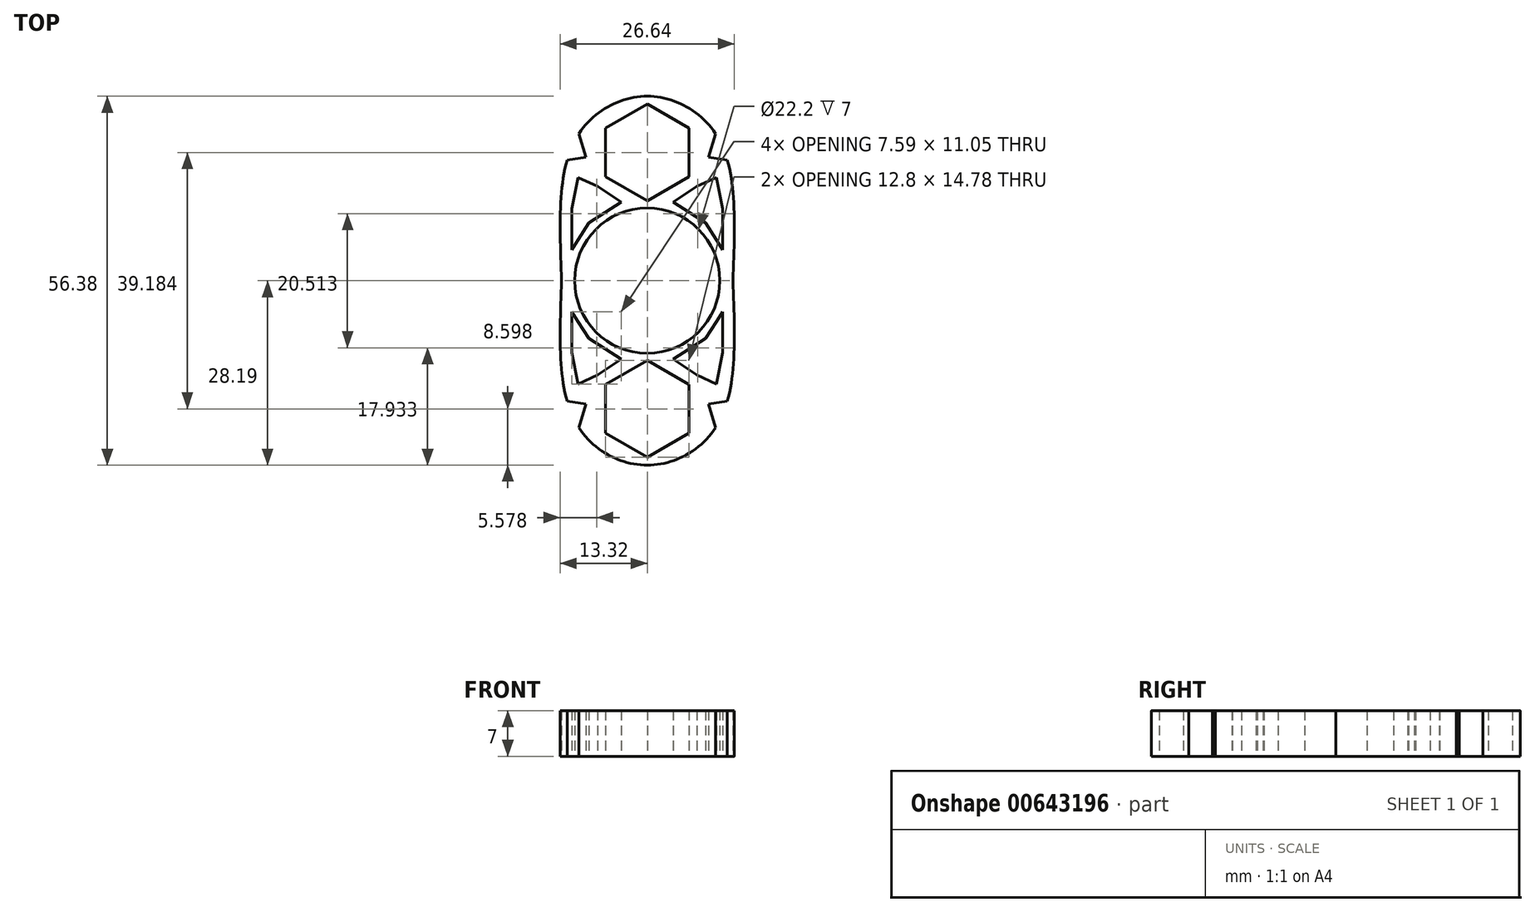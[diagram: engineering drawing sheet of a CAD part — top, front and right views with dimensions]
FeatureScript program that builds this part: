
annotation { "Feature Type Name" : "Feature", "Feature Type Description" : "" }
export const myFeature = defineFeature(function(context is Context, id is Id, definition is map)
    precondition{}
    {
        {
            var Q0;
            Q0=qCreatedBy(makeId("Top.planeOp"),FACE);
            var sketch = newSketch(context, id + "F0", { "sketchPlane" : qUnion([Q0])});
            skCircle(sketch, "E0", {"center": v(0, 0) * mm, "radius": 11.1 * mm});
            skCircle(sketch, "E1.cCircle", {"center": v(0, 19.6) * mm, "radius": 6.4 * mm, "construction": true});
            skLineSegment(sketch, "E1.0", {"start": v(6.4, 23.29) * mm, "end": v(6.4, 15.9) * mm});
            skLineSegment(sketch, "E1.1", {"start": v(6.4, 15.9) * mm, "end": v(0, 12.2) * mm});
            skLineSegment(sketch, "E1.2", {"start": v(0, 12.2) * mm, "end": v(-6.4, 15.9) * mm});
            skLineSegment(sketch, "E1.3", {"start": v(-6.4, 15.9) * mm, "end": v(-6.4, 23.29) * mm});
            skLineSegment(sketch, "E1.4", {"start": v(-6.4, 23.29) * mm, "end": v(0, 26.98) * mm});
            skLineSegment(sketch, "E1.5", {"start": v(0, 26.98) * mm, "end": v(6.4, 23.29) * mm});
            skPoint(sketch, "E1.0.midPoint", {"position": v(6.4, 19.6) * mm});
            skLineSegment(sketch, "E2", {"start": v(-40.43, 30) * mm, "end": v(39.47, 30) * mm, "construction": true});
            skLineSegment(sketch, "E3", {"start": v(39.47, 30) * mm, "end": v(39.47, -30) * mm, "construction": true});
            skLineSegment(sketch, "E4", {"start": v(39.47, -30) * mm, "end": v(-39.28, -30) * mm, "construction": true});
            skFitSpline(sketch, "E5", {"points": [v(0, 28.19) * mm, v(-10.7, 22.08) * mm, v(-13.1, 0) * mm], "startDerivative": vector(-28.16, 0.12) * mm, "endDerivative": vector(1.7, -45.3) * mm});
            skFitSpline(sketch, "E6.MirrorCS", {"points": [v(0, 28.19) * mm, v(10.7, 22.08) * mm, v(13.1, 0) * mm], "startDerivative": vector(28.16, 0.12) * mm, "endDerivative": vector(-1.7, -45.3) * mm});
            skFitSpline(sketch, "E7.MirrorCS", {"points": [v(0, -28.19) * mm, v(-10.7, -22.08) * mm, v(-13.1, 0) * mm], "startDerivative": vector(-28.16, -0.12) * mm, "endDerivative": vector(1.7, 45.3) * mm});
            skFitSpline(sketch, "E8.MirrorCS", {"points": [v(0, -28.19) * mm, v(10.7, -22.08) * mm, v(13.1, 0) * mm], "startDerivative": vector(28.16, -0.12) * mm, "endDerivative": vector(-1.7, 45.3) * mm});
            skLineSegment(sketch, "E9.MirrorCS", {"start": v(-6.4, -15.9) * mm, "end": v(-6.4, -23.29) * mm});
            skPoint(sketch, "E10.MirrorP", {"position": v(6.4, -19.6) * mm});
            skLineSegment(sketch, "E11.MirrorCS", {"start": v(6.4, -23.29) * mm, "end": v(6.4, -15.9) * mm});
            skCircle(sketch, "E12.MirrorC", {"center": v(0, -19.6) * mm, "radius": 6.4 * mm, "construction": true});
            skLineSegment(sketch, "E13.MirrorCS", {"start": v(0, -26.98) * mm, "end": v(6.4, -23.29) * mm});
            skLineSegment(sketch, "E14.MirrorCS", {"start": v(-6.4, -23.29) * mm, "end": v(0, -26.98) * mm});
            skLineSegment(sketch, "E15.MirrorCS", {"start": v(0, -12.2) * mm, "end": v(-6.4, -15.9) * mm});
            skLineSegment(sketch, "E16.MirrorCS", {"start": v(6.4, -15.9) * mm, "end": v(0, -12.2) * mm});
            skLineSegment(sketch, "E17", {"start": v(7.6, 14.42) * mm, "end": v(3.94, 12) * mm});
            skLineSegment(sketch, "E18", {"start": v(3.94, 12) * mm, "end": v(8.93, 8.83) * mm});
            skLineSegment(sketch, "E19", {"start": v(8.93, 8.83) * mm, "end": v(10.58, 6.26) * mm});
            skLineSegment(sketch, "E20", {"start": v(10.58, 6.26) * mm, "end": v(11.54, 4.73) * mm});
            skLineSegment(sketch, "E21", {"start": v(11.54, 4.73) * mm, "end": v(11.54, 11) * mm});
            skLineSegment(sketch, "E22", {"start": v(11.54, 11) * mm, "end": v(10.58, 15.78) * mm});
            skLineSegment(sketch, "E23", {"start": v(10.58, 15.78) * mm, "end": v(7.6, 14.42) * mm});
            skLineSegment(sketch, "E24.MirrorCS", {"start": v(-10.58, 6.26) * mm, "end": v(-11.54, 4.73) * mm});
            skLineSegment(sketch, "E25.MirrorCS", {"start": v(-10.58, 15.78) * mm, "end": v(-7.6, 14.42) * mm});
            skLineSegment(sketch, "E26.MirrorCS", {"start": v(-3.94, 12) * mm, "end": v(-8.93, 8.83) * mm});
            skLineSegment(sketch, "E27.MirrorCS", {"start": v(-7.6, 14.42) * mm, "end": v(-3.94, 12) * mm});
            skLineSegment(sketch, "E28.MirrorCS", {"start": v(-8.93, 8.83) * mm, "end": v(-10.58, 6.26) * mm});
            skLineSegment(sketch, "E29.MirrorCS", {"start": v(-11.54, 11) * mm, "end": v(-10.58, 15.78) * mm});
            skLineSegment(sketch, "E30.MirrorCS", {"start": v(-11.54, 4.73) * mm, "end": v(-11.54, 11) * mm});
            skLineSegment(sketch, "E31.MirrorCS", {"start": v(-10.58, -6.26) * mm, "end": v(-11.54, -4.73) * mm});
            skLineSegment(sketch, "E32.MirrorCS", {"start": v(-3.94, -12) * mm, "end": v(-8.93, -8.83) * mm});
            skLineSegment(sketch, "E33.MirrorCS", {"start": v(-11.54, -4.73) * mm, "end": v(-11.54, -11) * mm});
            skLineSegment(sketch, "E34.MirrorCS", {"start": v(-10.58, -15.78) * mm, "end": v(-7.6, -14.42) * mm});
            skLineSegment(sketch, "E35.MirrorCS", {"start": v(-8.93, -8.83) * mm, "end": v(-10.58, -6.26) * mm});
            skLineSegment(sketch, "E36.MirrorCS", {"start": v(-7.6, -14.42) * mm, "end": v(-3.94, -12) * mm});
            skLineSegment(sketch, "E37.MirrorCS", {"start": v(-11.54, -11) * mm, "end": v(-10.58, -15.78) * mm});
            skLineSegment(sketch, "E38.MirrorCS", {"start": v(10.58, -6.26) * mm, "end": v(11.54, -4.73) * mm});
            skLineSegment(sketch, "E39.MirrorCS", {"start": v(10.58, -15.78) * mm, "end": v(7.6, -14.42) * mm});
            skLineSegment(sketch, "E40.MirrorCS", {"start": v(8.93, -8.83) * mm, "end": v(10.58, -6.26) * mm});
            skLineSegment(sketch, "E41.MirrorCS", {"start": v(11.54, -4.73) * mm, "end": v(11.54, -11) * mm});
            skLineSegment(sketch, "E42.MirrorCS", {"start": v(11.54, -11) * mm, "end": v(10.58, -15.78) * mm});
            skLineSegment(sketch, "E43.MirrorCS", {"start": v(7.6, -14.42) * mm, "end": v(3.94, -12) * mm});
            skLineSegment(sketch, "E44.MirrorCS", {"start": v(3.94, -12) * mm, "end": v(8.93, -8.83) * mm});
            skLineSegment(sketch, "E45", {"start": v(-14.85, 18.06) * mm, "end": v(-9.4, 18.84) * mm});
            skLineSegment(sketch, "E46", {"start": v(-9.4, 18.84) * mm, "end": v(-11.31, 25.3) * mm});
            skLineSegment(sketch, "E47", {"start": v(-11.31, 25.3) * mm, "end": v(-14.85, 18.06) * mm});
            skLineSegment(sketch, "E48.MirrorCS", {"start": v(9.4, 18.84) * mm, "end": v(11.31, 25.3) * mm});
            skLineSegment(sketch, "E49.MirrorCS", {"start": v(11.31, 25.3) * mm, "end": v(14.85, 18.06) * mm});
            skLineSegment(sketch, "E50.MirrorCS", {"start": v(14.85, 18.06) * mm, "end": v(9.4, 18.84) * mm});
            skLineSegment(sketch, "E51.MirrorCS", {"start": v(-9.4, -18.84) * mm, "end": v(-11.31, -25.3) * mm});
            skLineSegment(sketch, "E52.MirrorCS", {"start": v(-11.31, -25.3) * mm, "end": v(-14.85, -18.06) * mm});
            skLineSegment(sketch, "E53.MirrorCS", {"start": v(-14.85, -18.06) * mm, "end": v(-9.4, -18.84) * mm});
            skLineSegment(sketch, "E54.MirrorCS", {"start": v(14.85, -18.06) * mm, "end": v(9.4, -18.84) * mm});
            skLineSegment(sketch, "E55.MirrorCS", {"start": v(11.31, -25.3) * mm, "end": v(14.85, -18.06) * mm});
            skLineSegment(sketch, "E56.MirrorCS", {"start": v(9.4, -18.84) * mm, "end": v(11.31, -25.3) * mm});
            skSolve(sketch);
        }
        {
            var Q0;
            Q0=makeQuery(id+"F0.imprint","IMPRINT",FACE,{"disambiguationData":[TD([[makeQuery(id+"F0.imprint","IMPRINT",EDGE,{"derivedFrom":sQuery(id+"F0.wireOp",EDGE,"E0")}),-1.0]])]});
            extrude(context, id + "F1", {"entities" : qUnion([Q0]), "depth" : 7 * mm, "offsetDistance" : 25 * mm});
        }
    });
